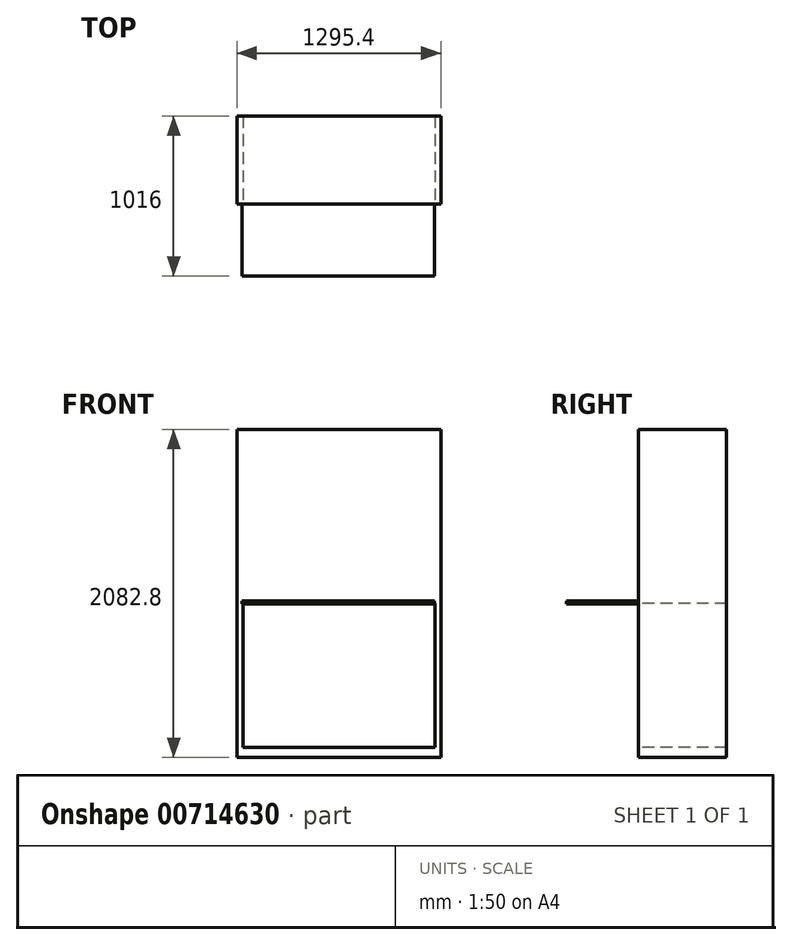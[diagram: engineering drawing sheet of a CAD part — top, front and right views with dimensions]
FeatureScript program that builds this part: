
annotation { "Feature Type Name" : "Feature", "Feature Type Description" : "" }
export const myFeature = defineFeature(function(context is Context, id is Id, definition is map)
    precondition{}
    {
        {
            var Q0;
            Q0=qCreatedBy(makeId("Front.planeOp"),FACE);
            var sketch = newSketch(context, id + "F0", { "sketchPlane" : qUnion([Q0])});
            skLineSegment(sketch, "E0.bottom", {"start": v(728.52, -1035.33) * mm, "end": v(-566.88, -1035.33) * mm});
            skLineSegment(sketch, "E0.top", {"start": v(728.52, 1047.47) * mm, "end": v(-566.88, 1047.47) * mm});
            skLineSegment(sketch, "E0.left", {"start": v(728.52, -1035.33) * mm, "end": v(728.52, 1047.47) * mm});
            skLineSegment(sketch, "E0.right", {"start": v(-566.88, -1035.33) * mm, "end": v(-566.88, 1047.47) * mm});
            skSolve(sketch);
        }
        {
            var Q0;
            Q0=makeQuery(id+"F0.imprint","IMPRINT",FACE,{"disambiguationData":[TD([[makeQuery(id+"F0.imprint","IMPRINT",EDGE,{"derivedFrom":sQuery(id+"F0.wireOp",EDGE,"E0.bottom")}),-1.0]])]});
            extrude(context, id + "F1", {"entities" : qUnion([Q0]), "oppositeDirection" : true, "depth" : 558.8 * mm, "offsetDistance" : 25.4 * mm});
        }
        {
            var Q0;
            Q0=makeQuery(id+"F1.opExtrude","CAP_FACE",FACE,{"disambiguationData":[OSD([sQuery(id+"F0.wireOp",EDGE,"E0.bottom"),sQuery(id+"F0.wireOp",EDGE,"E0.top"),sQuery(id+"F0.wireOp",EDGE,"E0.left"),sQuery(id+"F0.wireOp",EDGE,"E0.right")])],"isStart":true});
            var sketch = newSketch(context, id + "F2", { "sketchPlane" : qUnion([Q0])});
            skLineSegment(sketch, "E1.bottom", {"start": v(-528.78, 56.87) * mm, "end": v(690.42, 56.87) * mm});
            skLineSegment(sketch, "E1.top", {"start": v(-528.78, -44.73) * mm, "end": v(690.42, -44.73) * mm});
            skLineSegment(sketch, "E1.left", {"start": v(-528.78, 56.87) * mm, "end": v(-528.78, -44.73) * mm});
            skLineSegment(sketch, "E1.right", {"start": v(690.42, 56.87) * mm, "end": v(690.42, -44.73) * mm});
            skSolve(sketch);
        }
        {
            var Q0;
            Q0=makeQuery(id+"F2.imprint","IMPRINT",FACE,{"disambiguationData":[TD([[makeQuery(id+"F2.imprint","IMPRINT",EDGE,{"derivedFrom":sQuery(id+"F2.wireOp",EDGE,"E1.bottom")}),1.0]])]});
            var sketch = newSketch(context, id + "F3", { "sketchPlane" : qUnion([Q0])});
            skLineSegment(sketch, "E2.bottom", {"start": v(-528.78, -57.43) * mm, "end": v(690.42, -57.43) * mm});
            skLineSegment(sketch, "E2.top", {"start": v(-528.78, -971.83) * mm, "end": v(690.42, -971.83) * mm});
            skLineSegment(sketch, "E2.left", {"start": v(-528.78, -57.43) * mm, "end": v(-528.78, -971.83) * mm});
            skLineSegment(sketch, "E2.right", {"start": v(690.42, -57.43) * mm, "end": v(690.42, -971.83) * mm});
            skSolve(sketch);
        }
        {
            var Q0;
            Q0=makeQuery(id+"F2.imprint","IMPRINT",FACE,{"disambiguationData":[TD([[makeQuery(id+"F2.imprint","IMPRINT",EDGE,{"derivedFrom":sQuery(id+"F2.wireOp",EDGE,"E1.bottom")}),1.0]])]});
            var sketch = newSketch(context, id + "F4", { "sketchPlane" : qUnion([Q0])});
            skLineSegment(sketch, "E3.bottom", {"start": v(690.42, 564.87) * mm, "end": v(-528.78, 564.87) * mm});
            skLineSegment(sketch, "E3.top", {"start": v(690.42, 895.07) * mm, "end": v(-528.78, 895.07) * mm});
            skLineSegment(sketch, "E3.left", {"start": v(690.42, 564.87) * mm, "end": v(690.42, 895.07) * mm});
            skLineSegment(sketch, "E3.right", {"start": v(-528.78, 564.87) * mm, "end": v(-528.78, 895.07) * mm});
            skSolve(sketch);
        }
        {
            var Q0;
            Q0=makeQuery(id+"F2.imprint","IMPRINT",FACE,{"disambiguationData":[TD([[makeQuery(id+"F2.imprint","IMPRINT",EDGE,{"derivedFrom":sQuery(id+"F2.wireOp",EDGE,"E1.bottom")}),1.0]])]});
            var sketch = newSketch(context, id + "F5", { "sketchPlane" : qUnion([Q0])});
            skLineSegment(sketch, "E4.bottom", {"start": v(690.42, 552.17) * mm, "end": v(-528.78, 552.17) * mm});
            skLineSegment(sketch, "E4.top", {"start": v(690.42, 374.37) * mm, "end": v(-528.78, 374.37) * mm});
            skLineSegment(sketch, "E4.left", {"start": v(690.42, 552.17) * mm, "end": v(690.42, 374.37) * mm});
            skLineSegment(sketch, "E4.right", {"start": v(-528.78, 552.17) * mm, "end": v(-528.78, 374.37) * mm});
            skSolve(sketch);
        }
        {
            var Q0;
            Q0=makeQuery(id+"F5.imprint","IMPRINT",FACE,{"disambiguationData":[TD([[makeQuery(id+"F5.imprint","IMPRINT",EDGE,{"derivedFrom":sQuery(id+"F5.wireOp",EDGE,"E4.bottom")}),-1.0]])]});
            var sketch = newSketch(context, id + "F6", { "sketchPlane" : qUnion([Q0])});
            skLineSegment(sketch, "E5.bottom", {"start": v(690.42, 361.67) * mm, "end": v(-528.78, 361.67) * mm});
            skLineSegment(sketch, "E5.top", {"start": v(690.42, 183.87) * mm, "end": v(-528.78, 183.87) * mm});
            skLineSegment(sketch, "E5.left", {"start": v(690.42, 361.67) * mm, "end": v(690.42, 183.87) * mm});
            skLineSegment(sketch, "E5.right", {"start": v(-528.78, 361.67) * mm, "end": v(-528.78, 183.87) * mm});
            skSolve(sketch);
        }
        {
            var Q0;
            Q0=makeQuery(id+"F5.imprint","IMPRINT",FACE,{"disambiguationData":[TD([[makeQuery(id+"F5.imprint","IMPRINT",EDGE,{"derivedFrom":sQuery(id+"F5.wireOp",EDGE,"E4.bottom")}),-1.0]])]});
            var sketch = newSketch(context, id + "F7", { "sketchPlane" : qUnion([Q0])});
            skLineSegment(sketch, "E6.bottom", {"start": v(690.42, 171.17) * mm, "end": v(-528.78, 171.17) * mm});
            skLineSegment(sketch, "E6.top", {"start": v(690.42, 69.57) * mm, "end": v(-528.78, 69.57) * mm});
            skLineSegment(sketch, "E6.left", {"start": v(690.42, 171.17) * mm, "end": v(690.42, 69.57) * mm});
            skLineSegment(sketch, "E6.right", {"start": v(-528.78, 171.17) * mm, "end": v(-528.78, 69.57) * mm});
            skSolve(sketch);
        }
        {
            var Q0;
            Q0=makeQuery(id+"F7.imprint","IMPRINT",FACE,{"disambiguationData":[TD([[makeQuery(id+"F7.imprint","IMPRINT",EDGE,{"derivedFrom":sQuery(id+"F7.wireOp",EDGE,"E6.bottom")}),-1.0]])]});
            var sketch = newSketch(context, id + "F8", { "sketchPlane" : qUnion([Q0])});
            skLineSegment(sketch, "E7.bottom", {"start": v(690.42, -53) * mm, "end": v(-528.78, -53) * mm});
            skLineSegment(sketch, "E7.top", {"start": v(690.42, -510.2) * mm, "end": v(-528.78, -510.2) * mm});
            skLineSegment(sketch, "E7.left", {"start": v(690.42, -53) * mm, "end": v(690.42, -510.2) * mm});
            skLineSegment(sketch, "E7.right", {"start": v(-528.78, -53) * mm, "end": v(-528.78, -510.2) * mm});
            skSolve(sketch);
        }
        {
            var Q0;
            Q0 = qSketchRegion(id + "F3", true);
            extrude(context, id + "F9", {"entities" : qUnion([Q0]), "operationType" : NewBodyOperationType.REMOVE, "endBound" : BoundingType.UP_TO_NEXT, "oppositeDirection" : true, "depth" : 25.4 * mm, "offsetDistance" : 25.4 * mm});
        }
        {
            var Q0;
            Q0=makeQuery(id+"F4.imprint","IMPRINT",FACE,{"disambiguationData":[TD([[makeQuery(id+"F4.imprint","IMPRINT",EDGE,{"derivedFrom":sQuery(id+"F4.wireOp",EDGE,"E3.bottom")}),1.0]])]});
            var sketch = newSketch(context, id + "F10", { "sketchPlane" : qUnion([Q0])});
            skLineSegment(sketch, "E8.bottom", {"start": v(-533.96, -61.32) * mm, "end": v(689.53, -61.32) * mm});
            skLineSegment(sketch, "E8.top", {"start": v(-533.96, -42.22) * mm, "end": v(689.53, -42.22) * mm});
            skLineSegment(sketch, "E8.left", {"start": v(-533.96, -61.32) * mm, "end": v(-533.96, -42.22) * mm});
            skLineSegment(sketch, "E8.right", {"start": v(689.53, -61.32) * mm, "end": v(689.53, -42.22) * mm});
            skSolve(sketch);
        }
        {
            var Q0;
            Q0 = qSketchRegion(id + "F10", true);
            extrude(context, id + "F11", {"entities" : qUnion([Q0]), "operationType" : NewBodyOperationType.ADD, "depth" : 457.2 * mm, "offsetDistance" : 25.4 * mm});
        }
    });
